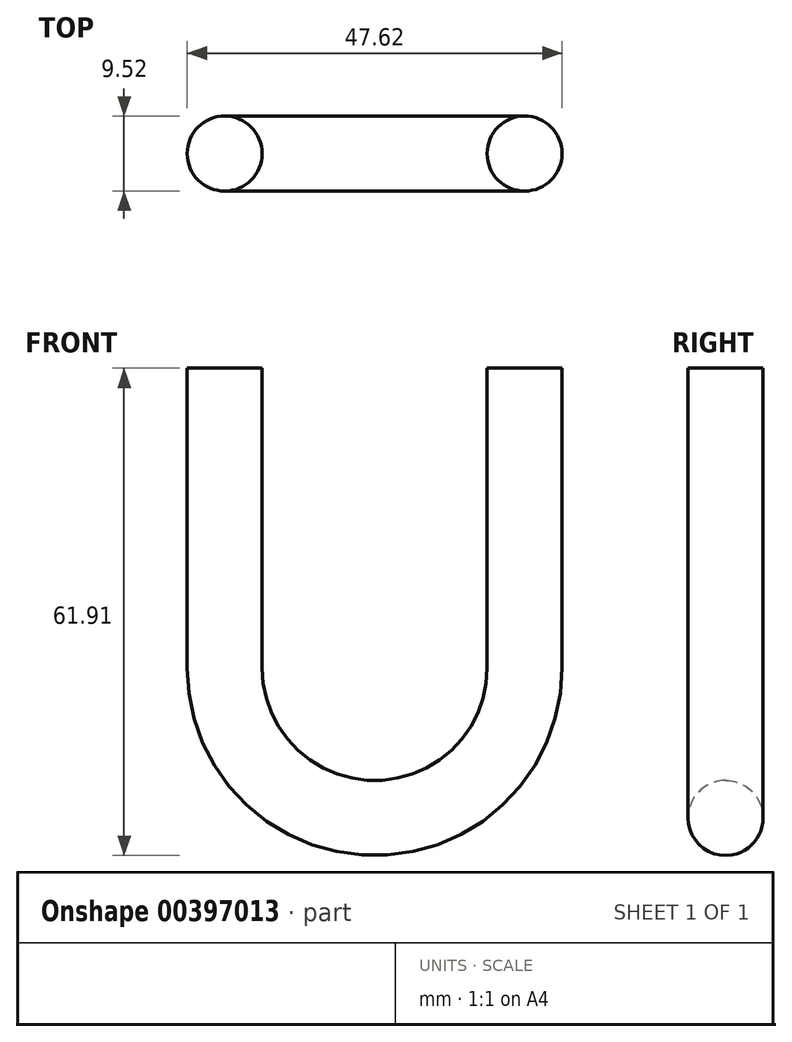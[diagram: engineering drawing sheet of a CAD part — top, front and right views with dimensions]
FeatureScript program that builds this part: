
annotation { "Feature Type Name" : "Feature", "Feature Type Description" : "" }
export const myFeature = defineFeature(function(context is Context, id is Id, definition is map)
    precondition{}
    {
        {
            var Q0;
            Q0=qCreatedBy(makeId("Front.planeOp"),FACE);
            var sketch = newSketch(context, id + "F0", { "sketchPlane" : qUnion([Q0])});
            skLineSegment(sketch, "E0", {"start": v(0, 0) * mm, "end": v(0, -38.1) * mm});
            skArc(sketch, "E1", {"start": v(0, -38.1) * mm, "mid": v(-19.05, -57.15) * mm, "end": v(-38.1, -38.1) * mm});
            skLineSegment(sketch, "E2", {"start": v(-38.1, -38.1) * mm, "end": v(-38.1, 0) * mm});
            skSolve(sketch);
        }
        {
            var Q0;
            Q0=qCreatedBy(makeId("Top.planeOp"),FACE);
            var sketch = newSketch(context, id + "F1", { "sketchPlane" : qUnion([Q0])});
            skCircle(sketch, "E3", {"center": v(-38.1, 0) * mm, "radius": 4.76 * mm});
            skSolve(sketch);
        }
        {
            var Q0;
            Q0=makeQuery(id+"F1.imprint","IMPRINT",FACE,{"disambiguationData":[TD([[makeQuery(id+"F1.imprint","IMPRINT",EDGE,{"derivedFrom":sQuery(id+"F1.wireOp",EDGE,"E3")}),1.0]])]});
            var Q1;
            Q1 = qConstructionFilter(qBodyType(qCreatedBy(id + "F0" ,EDGE), BodyType.WIRE), ConstructionObject.NO);
            sweep(context, id + "F2", {"profiles" : qUnion([Q0]), "path" : qUnion([Q1])});
        }
    });
